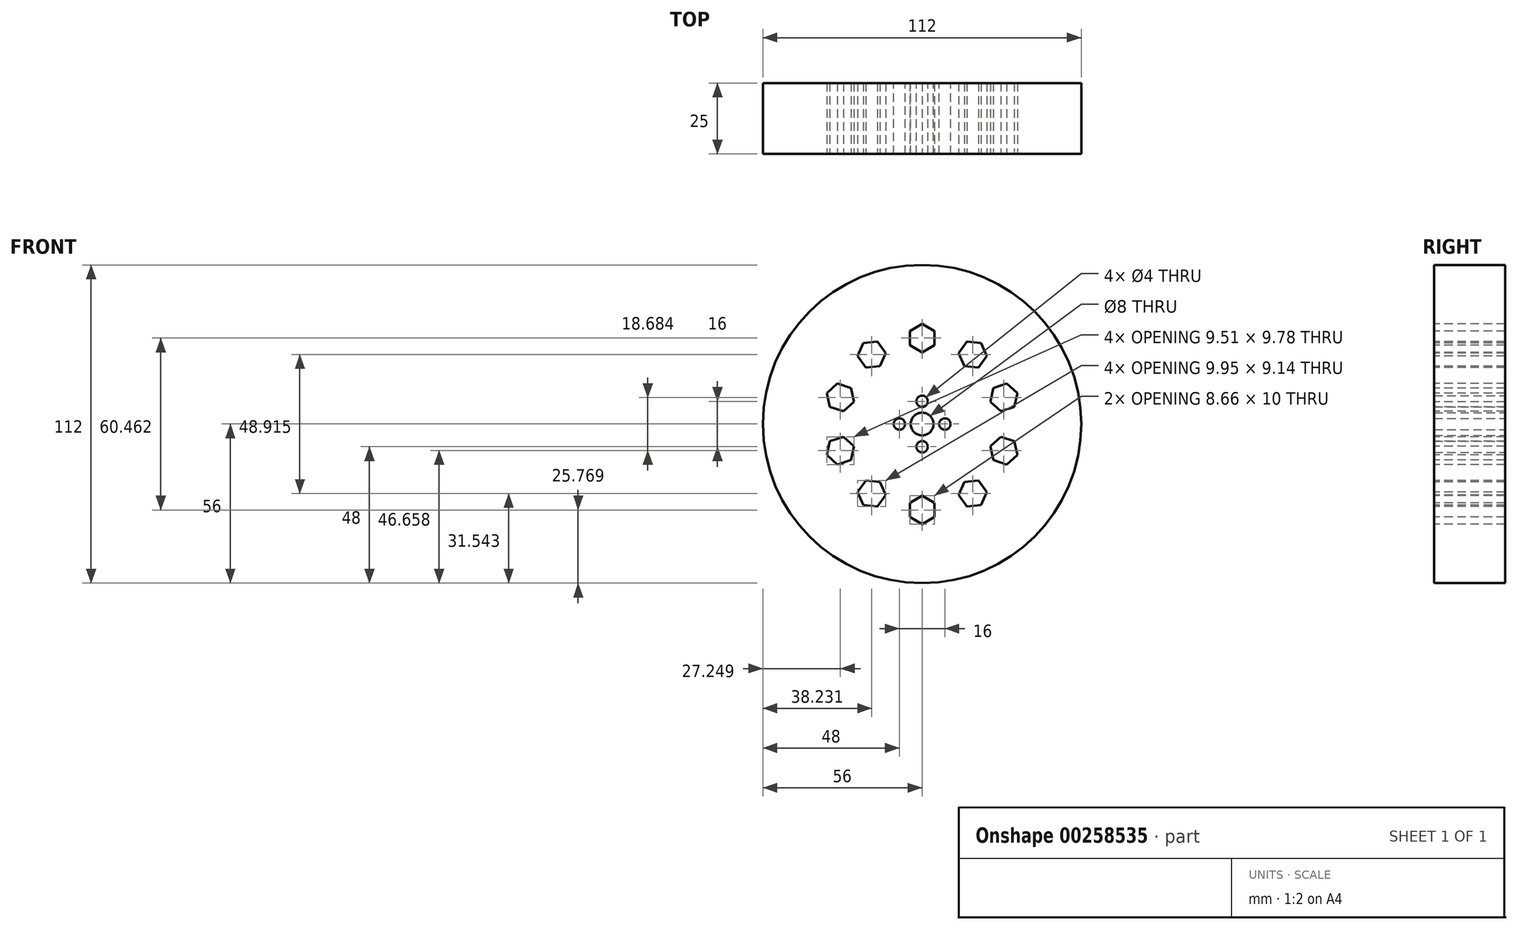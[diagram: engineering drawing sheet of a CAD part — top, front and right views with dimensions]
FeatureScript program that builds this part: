
annotation { "Feature Type Name" : "Feature", "Feature Type Description" : "" }
export const myFeature = defineFeature(function(context is Context, id is Id, definition is map)
    precondition{}
    {
        {
            var Q0;
            Q0=qCreatedBy(makeId("Front.planeOp"),FACE);
            var sketch = newSketch(context, id + "F0", { "sketchPlane" : qUnion([Q0])});
            skCircle(sketch, "E0", {"center": v(-66, 0) * mm, "radius": 16 * mm});
            skCircle(sketch, "E1", {"center": v(66, 0) * mm, "radius": 16 * mm});
            skCircle(sketch, "E2", {"center": v(-66, 0) * mm, "radius": 21 * mm});
            skCircle(sketch, "E3", {"center": v(66, 0) * mm, "radius": 21 * mm});
            skCircle(sketch, "E4", {"center": v(-66, 0) * mm, "radius": 56 * mm});
            skCircle(sketch, "E5", {"center": v(66, 0) * mm, "radius": 56 * mm});
            skLineSegment(sketch, "E6", {"start": v(-66, 0) * mm, "end": v(-66, 8) * mm, "construction": true});
            skCircle(sketch, "E7", {"center": v(-66, 8) * mm, "radius": 2 * mm});
            skCircle(sketch, "E8", {"center": v(-66, 0) * mm, "radius": 4 * mm});
            skCircle(sketch, "E9.1.0", {"center": v(-74, 0) * mm, "radius": 2 * mm});
            skCircle(sketch, "E9.2.0", {"center": v(-66, -8) * mm, "radius": 2 * mm});
            skCircle(sketch, "E9.3.0", {"center": v(-58, 0) * mm, "radius": 2 * mm});
            skSolve(sketch);
        }
        {
            var Q0;
            Q0=qCreatedBy(makeId("Front.planeOp"),FACE);
            var sketch = newSketch(context, id + "F1", { "sketchPlane" : qUnion([Q0])});
            skCircle(sketch, "E10.cCircle", {"center": v(-66, 30.23) * mm, "radius": 5 * mm, "construction": true});
            skLineSegment(sketch, "E10.0", {"start": v(-61.67, 27.73) * mm, "end": v(-66, 25.23) * mm});
            skLineSegment(sketch, "E10.1", {"start": v(-66, 25.23) * mm, "end": v(-70.33, 27.73) * mm});
            skLineSegment(sketch, "E10.2", {"start": v(-70.33, 27.73) * mm, "end": v(-70.33, 32.73) * mm});
            skLineSegment(sketch, "E10.3", {"start": v(-70.33, 32.73) * mm, "end": v(-66, 35.23) * mm});
            skLineSegment(sketch, "E10.4", {"start": v(-66, 35.23) * mm, "end": v(-61.67, 32.73) * mm});
            skLineSegment(sketch, "E10.5", {"start": v(-61.67, 32.73) * mm, "end": v(-61.67, 27.73) * mm});
            skPoint(sketch, "E11", {"position": v(-66, 0) * mm});
            skCircle(sketch, "E12.1.0", {"center": v(-83.77, 24.46) * mm, "radius": 5 * mm, "construction": true});
            skLineSegment(sketch, "E12.1.1", {"start": v(-81.74, 29.03) * mm, "end": v(-78.8, 24.98) * mm});
            skLineSegment(sketch, "E12.1.2", {"start": v(-86.7, 28.5) * mm, "end": v(-81.74, 29.03) * mm});
            skLineSegment(sketch, "E12.1.3", {"start": v(-88.74, 23.93) * mm, "end": v(-86.7, 28.5) * mm});
            skLineSegment(sketch, "E12.1.4", {"start": v(-85.8, 19.89) * mm, "end": v(-88.74, 23.93) * mm});
            skLineSegment(sketch, "E12.1.5", {"start": v(-80.83, 20.41) * mm, "end": v(-85.8, 19.89) * mm});
            skLineSegment(sketch, "E12.1.6", {"start": v(-78.8, 24.98) * mm, "end": v(-80.83, 20.41) * mm});
            skCircle(sketch, "E12.2.0", {"center": v(-94.75, 9.34) * mm, "radius": 5 * mm, "construction": true});
            skLineSegment(sketch, "E12.2.1", {"start": v(-95.8, 14.23) * mm, "end": v(-91.04, 12.69) * mm});
            skLineSegment(sketch, "E12.2.2", {"start": v(-99.5, 10.89) * mm, "end": v(-95.8, 14.23) * mm});
            skLineSegment(sketch, "E12.2.3", {"start": v(-98.47, 6) * mm, "end": v(-99.5, 10.89) * mm});
            skLineSegment(sketch, "E12.2.4", {"start": v(-93.71, 4.45) * mm, "end": v(-98.47, 6) * mm});
            skLineSegment(sketch, "E12.2.5", {"start": v(-90, 7.8) * mm, "end": v(-93.71, 4.45) * mm});
            skLineSegment(sketch, "E12.2.6", {"start": v(-91.04, 12.69) * mm, "end": v(-90, 7.8) * mm});
            skCircle(sketch, "E12.3.0", {"center": v(-94.75, -9.34) * mm, "radius": 5 * mm, "construction": true});
            skLineSegment(sketch, "E12.3.1", {"start": v(-98.47, -6) * mm, "end": v(-93.71, -4.45) * mm});
            skLineSegment(sketch, "E12.3.2", {"start": v(-99.5, -10.89) * mm, "end": v(-98.47, -6) * mm});
            skLineSegment(sketch, "E12.3.3", {"start": v(-95.8, -14.23) * mm, "end": v(-99.5, -10.89) * mm});
            skLineSegment(sketch, "E12.3.4", {"start": v(-91.04, -12.69) * mm, "end": v(-95.8, -14.23) * mm});
            skLineSegment(sketch, "E12.3.5", {"start": v(-90, -7.8) * mm, "end": v(-91.04, -12.69) * mm});
            skLineSegment(sketch, "E12.3.6", {"start": v(-93.71, -4.45) * mm, "end": v(-90, -7.8) * mm});
            skCircle(sketch, "E12.4.0", {"center": v(-83.77, -24.46) * mm, "radius": 5 * mm, "construction": true});
            skLineSegment(sketch, "E12.4.1", {"start": v(-88.74, -23.93) * mm, "end": v(-85.8, -19.89) * mm});
            skLineSegment(sketch, "E12.4.2", {"start": v(-86.7, -28.5) * mm, "end": v(-88.74, -23.93) * mm});
            skLineSegment(sketch, "E12.4.3", {"start": v(-81.74, -29.03) * mm, "end": v(-86.7, -28.5) * mm});
            skLineSegment(sketch, "E12.4.4", {"start": v(-78.8, -24.98) * mm, "end": v(-81.74, -29.03) * mm});
            skLineSegment(sketch, "E12.4.5", {"start": v(-80.83, -20.41) * mm, "end": v(-78.8, -24.98) * mm});
            skLineSegment(sketch, "E12.4.6", {"start": v(-85.8, -19.89) * mm, "end": v(-80.83, -20.41) * mm});
            skCircle(sketch, "E12.5.0", {"center": v(-66, -30.23) * mm, "radius": 5 * mm, "construction": true});
            skLineSegment(sketch, "E12.5.1", {"start": v(-70.33, -32.73) * mm, "end": v(-70.33, -27.73) * mm});
            skLineSegment(sketch, "E12.5.2", {"start": v(-66, -35.23) * mm, "end": v(-70.33, -32.73) * mm});
            skLineSegment(sketch, "E12.5.3", {"start": v(-61.67, -32.73) * mm, "end": v(-66, -35.23) * mm});
            skLineSegment(sketch, "E12.5.4", {"start": v(-61.67, -27.73) * mm, "end": v(-61.67, -32.73) * mm});
            skLineSegment(sketch, "E12.5.5", {"start": v(-66, -25.23) * mm, "end": v(-61.67, -27.73) * mm});
            skLineSegment(sketch, "E12.5.6", {"start": v(-70.33, -27.73) * mm, "end": v(-66, -25.23) * mm});
            skCircle(sketch, "E12.6.0", {"center": v(-48.23, -24.46) * mm, "radius": 5 * mm, "construction": true});
            skLineSegment(sketch, "E12.6.1", {"start": v(-50.26, -29.03) * mm, "end": v(-53.2, -24.98) * mm});
            skLineSegment(sketch, "E12.6.2", {"start": v(-45.3, -28.5) * mm, "end": v(-50.26, -29.03) * mm});
            skLineSegment(sketch, "E12.6.3", {"start": v(-43.26, -23.93) * mm, "end": v(-45.3, -28.5) * mm});
            skLineSegment(sketch, "E12.6.4", {"start": v(-46.2, -19.89) * mm, "end": v(-43.26, -23.93) * mm});
            skLineSegment(sketch, "E12.6.5", {"start": v(-51.17, -20.41) * mm, "end": v(-46.2, -19.89) * mm});
            skLineSegment(sketch, "E12.6.6", {"start": v(-53.2, -24.98) * mm, "end": v(-51.17, -20.41) * mm});
            skCircle(sketch, "E12.7.0", {"center": v(-37.25, -9.34) * mm, "radius": 5 * mm, "construction": true});
            skLineSegment(sketch, "E12.7.1", {"start": v(-36.2, -14.23) * mm, "end": v(-40.96, -12.69) * mm});
            skLineSegment(sketch, "E12.7.2", {"start": v(-32.5, -10.89) * mm, "end": v(-36.2, -14.23) * mm});
            skLineSegment(sketch, "E12.7.3", {"start": v(-33.53, -6) * mm, "end": v(-32.5, -10.89) * mm});
            skLineSegment(sketch, "E12.7.4", {"start": v(-38.29, -4.45) * mm, "end": v(-33.53, -6) * mm});
            skLineSegment(sketch, "E12.7.5", {"start": v(-42, -7.8) * mm, "end": v(-38.29, -4.45) * mm});
            skLineSegment(sketch, "E12.7.6", {"start": v(-40.96, -12.69) * mm, "end": v(-42, -7.8) * mm});
            skCircle(sketch, "E12.8.0", {"center": v(-37.25, 9.34) * mm, "radius": 5 * mm, "construction": true});
            skLineSegment(sketch, "E12.8.1", {"start": v(-33.53, 6) * mm, "end": v(-38.29, 4.45) * mm});
            skLineSegment(sketch, "E12.8.2", {"start": v(-32.5, 10.89) * mm, "end": v(-33.53, 6) * mm});
            skLineSegment(sketch, "E12.8.3", {"start": v(-36.2, 14.23) * mm, "end": v(-32.5, 10.89) * mm});
            skLineSegment(sketch, "E12.8.4", {"start": v(-40.96, 12.69) * mm, "end": v(-36.2, 14.23) * mm});
            skLineSegment(sketch, "E12.8.5", {"start": v(-42, 7.8) * mm, "end": v(-40.96, 12.69) * mm});
            skLineSegment(sketch, "E12.8.6", {"start": v(-38.29, 4.45) * mm, "end": v(-42, 7.8) * mm});
            skCircle(sketch, "E12.9.0", {"center": v(-48.23, 24.46) * mm, "radius": 5 * mm, "construction": true});
            skLineSegment(sketch, "E12.9.1", {"start": v(-43.26, 23.93) * mm, "end": v(-46.2, 19.89) * mm});
            skLineSegment(sketch, "E12.9.2", {"start": v(-45.3, 28.5) * mm, "end": v(-43.26, 23.93) * mm});
            skLineSegment(sketch, "E12.9.3", {"start": v(-50.26, 29.03) * mm, "end": v(-45.3, 28.5) * mm});
            skLineSegment(sketch, "E12.9.4", {"start": v(-53.2, 24.98) * mm, "end": v(-50.26, 29.03) * mm});
            skLineSegment(sketch, "E12.9.5", {"start": v(-51.17, 20.41) * mm, "end": v(-53.2, 24.98) * mm});
            skLineSegment(sketch, "E12.9.6", {"start": v(-46.2, 19.89) * mm, "end": v(-51.17, 20.41) * mm});
            skCircle(sketch, "E13", {"center": v(-66, 0) * mm, "radius": 8 * mm, "construction": true});
            skCircle(sketch, "E14.cCircle", {"center": v(-51.11, 41.6) * mm, "radius": 5 * mm, "construction": true});
            skLineSegment(sketch, "E14.0", {"start": v(-51.11, 46.6) * mm, "end": v(-46.78, 44.1) * mm});
            skLineSegment(sketch, "E14.1", {"start": v(-46.78, 44.1) * mm, "end": v(-46.78, 39.1) * mm});
            skLineSegment(sketch, "E14.2", {"start": v(-46.78, 39.1) * mm, "end": v(-51.11, 36.6) * mm});
            skLineSegment(sketch, "E14.3", {"start": v(-51.11, 36.6) * mm, "end": v(-55.44, 39.1) * mm});
            skLineSegment(sketch, "E14.4", {"start": v(-55.44, 39.1) * mm, "end": v(-55.44, 44.1) * mm});
            skLineSegment(sketch, "E14.5", {"start": v(-55.44, 44.1) * mm, "end": v(-51.11, 46.6) * mm});
            skSolve(sketch);
        }
        {
            var Q0;
            Q0=makeQuery(id+"F0.imprint","IMPRINT",FACE,{"disambiguationData":[TD([[makeQuery(id+"F0.imprint","IMPRINT",EDGE,{"derivedFrom":sQuery(id+"F0.wireOp",EDGE,"E2")}),-1.0]])]});
            extrude(context, id + "F2", {"entities" : qUnion([Q0]), "endBound" : BoundingType.SYMMETRIC, "depth" : 25 * mm});
        }
        {
            var Q0;
            Q0=makeQuery(id+"F1.imprint","IMPRINT",FACE,{"disambiguationData":[TD([[makeQuery(id+"F1.imprint","IMPRINT",EDGE,{"derivedFrom":sQuery(id+"F1.wireOp",EDGE,"E12.2.1")}),-1.0]])]});
            var Q1;
            Q1=makeQuery(id+"F1.imprint","IMPRINT",FACE,{"disambiguationData":[TD([[makeQuery(id+"F1.imprint","IMPRINT",EDGE,{"derivedFrom":sQuery(id+"F1.wireOp",EDGE,"E12.1.1")}),-1.0]])]});
            var Q2;
            Q2=makeQuery(id+"F1.imprint","IMPRINT",FACE,{"disambiguationData":[TD([[makeQuery(id+"F1.imprint","IMPRINT",EDGE,{"derivedFrom":sQuery(id+"F1.wireOp",EDGE,"E10.0")}),-1.0]])]});
            var Q3;
            Q3=makeQuery(id+"F1.imprint","IMPRINT",FACE,{"disambiguationData":[TD([[makeQuery(id+"F1.imprint","IMPRINT",EDGE,{"derivedFrom":sQuery(id+"F1.wireOp",EDGE,"E12.9.1")}),-1.0]])]});
            var Q4;
            Q4=makeQuery(id+"F1.imprint","IMPRINT",FACE,{"disambiguationData":[TD([[makeQuery(id+"F1.imprint","IMPRINT",EDGE,{"derivedFrom":sQuery(id+"F1.wireOp",EDGE,"E12.8.1")}),-1.0]])]});
            var Q5;
            Q5=makeQuery(id+"F1.imprint","IMPRINT",FACE,{"disambiguationData":[TD([[makeQuery(id+"F1.imprint","IMPRINT",EDGE,{"derivedFrom":sQuery(id+"F1.wireOp",EDGE,"E12.7.1")}),-1.0]])]});
            var Q6;
            Q6=makeQuery(id+"F1.imprint","IMPRINT",FACE,{"disambiguationData":[TD([[makeQuery(id+"F1.imprint","IMPRINT",EDGE,{"derivedFrom":sQuery(id+"F1.wireOp",EDGE,"E12.6.1")}),-1.0]])]});
            var Q7;
            Q7=makeQuery(id+"F1.imprint","IMPRINT",FACE,{"disambiguationData":[TD([[makeQuery(id+"F1.imprint","IMPRINT",EDGE,{"derivedFrom":sQuery(id+"F1.wireOp",EDGE,"E12.5.1")}),-1.0]])]});
            var Q8;
            Q8=makeQuery(id+"F1.imprint","IMPRINT",FACE,{"disambiguationData":[TD([[makeQuery(id+"F1.imprint","IMPRINT",EDGE,{"derivedFrom":sQuery(id+"F1.wireOp",EDGE,"E12.4.1")}),-1.0]])]});
            var Q9;
            Q9=makeQuery(id+"F1.imprint","IMPRINT",FACE,{"disambiguationData":[TD([[makeQuery(id+"F1.imprint","IMPRINT",EDGE,{"derivedFrom":sQuery(id+"F1.wireOp",EDGE,"E12.3.1")}),-1.0]])]});
            extrude(context, id + "F3", {"entities" : qUnion([Q0, Q1, Q2, Q3, Q4, Q5, Q6, Q7, Q8, Q9]), "operationType" : NewBodyOperationType.REMOVE, "endBound" : BoundingType.SYMMETRIC, "oppositeDirection" : true, "depth" : 50 * mm});
        }
        {
            var Q0;
            Q0=makeQuery(id+"F0.imprint","IMPRINT",FACE,{"disambiguationData":[TD([[makeQuery(id+"F0.imprint","IMPRINT",EDGE,{"derivedFrom":sQuery(id+"F0.wireOp",EDGE,"E0")}),-1.0]])]});
            var Q1;
            Q1=makeQuery(id+"F0.imprint","IMPRINT",FACE,{"disambiguationData":[TD([[makeQuery(id+"F0.imprint","IMPRINT",EDGE,{"derivedFrom":sQuery(id+"F0.wireOp",EDGE,"E0")}),1.0]])]});
            extrude(context, id + "F4", {"entities" : qUnion([Q0, Q1]), "operationType" : NewBodyOperationType.ADD, "endBound" : BoundingType.SYMMETRIC, "depth" : 25 * mm});
        }
    });
